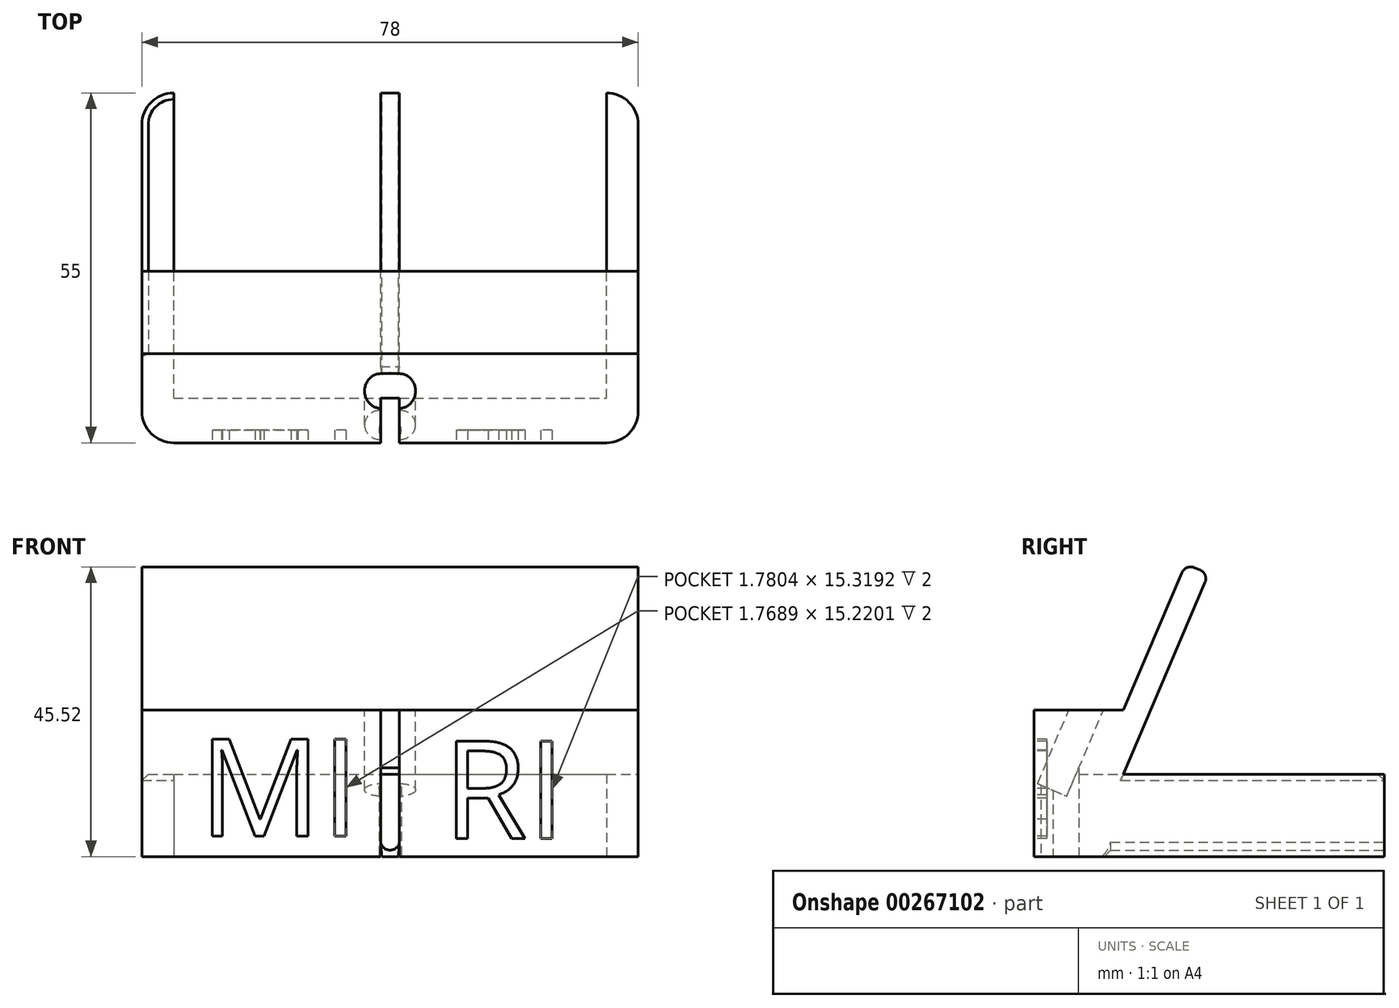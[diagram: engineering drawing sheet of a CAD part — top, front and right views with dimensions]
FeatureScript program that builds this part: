
annotation { "Feature Type Name" : "Feature", "Feature Type Description" : "" }
export const myFeature = defineFeature(function(context is Context, id is Id, definition is map)
    precondition{}
    {
        {
            var Q0;
            Q0=qCreatedBy(makeId("Top.planeOp"),FACE);
            var sketch = newSketch(context, id + "F0", { "sketchPlane" : qUnion([Q0])});
            skLineSegment(sketch, "E0.bottom", {"start": v(-34, 27.5) * mm, "end": v(34, 27.5) * mm});
            skLineSegment(sketch, "E0.top", {"start": v(-34, -27.5) * mm, "end": v(34, -27.5) * mm});
            skLineSegment(sketch, "E0.left", {"start": v(-39, 22.5) * mm, "end": v(-39, -22.5) * mm});
            skLineSegment(sketch, "E0.right", {"start": v(39, 22.5) * mm, "end": v(39, -22.5) * mm});
            skPoint(sketch, "E1.visualSharp", {"position": v(-39, 27.5) * mm});
            skArc(sketch, "E1.filletArc", {"start": v(-34, 27.5) * mm, "mid": v(-37.54, 26.04) * mm, "end": v(-39, 22.5) * mm});
            skPoint(sketch, "E2.visualSharp", {"position": v(39, 27.5) * mm});
            skArc(sketch, "E2.filletArc", {"start": v(39, 22.5) * mm, "mid": v(37.54, 26.04) * mm, "end": v(34, 27.5) * mm});
            skPoint(sketch, "E3.visualSharp", {"position": v(39, -27.5) * mm});
            skArc(sketch, "E3.filletArc", {"start": v(34, -27.5) * mm, "mid": v(37.54, -26.04) * mm, "end": v(39, -22.5) * mm});
            skPoint(sketch, "E4.visualSharp", {"position": v(-39, -27.5) * mm});
            skArc(sketch, "E4.filletArc", {"start": v(-39, -22.5) * mm, "mid": v(-37.54, -26.04) * mm, "end": v(-34, -27.5) * mm});
            skLineSegment(sketch, "E5", {"start": v(0, 27.5) * mm, "end": v(0, -27.5) * mm, "construction": true});
            skSolve(sketch);
        }
        {
            var Q0;
            Q0=makeQuery(id+"F0.imprint","IMPRINT",FACE,{"disambiguationData":[TD([[makeQuery(id+"F0.imprint","IMPRINT",EDGE,{"derivedFrom":sQuery(id+"F0.wireOp",EDGE,"E0.bottom")}),-1.0]])]});
            extrude(context, id + "F1", {"entities" : qUnion([Q0]), "depth" : 50 * mm});
        }
        {
            var Q0;
            Q0=makeQuery(id+"F1.opExtrude","SWEPT_FACE",FACE,{"disambiguationData":[OSD([sQuery(id+"F0.wireOp",EDGE,"E0.right")])]});
            var sketch = newSketch(context, id + "F2", { "sketchPlane" : qUnion([Q0])});
            skLineSegment(sketch, "E6", {"start": v(-27.5, 0) * mm, "end": v(-27.5, 23) * mm, "construction": true});
            skLineSegment(sketch, "E7", {"start": v(-27.5, 23) * mm, "end": v(-13.5, 23) * mm});
            skLineSegment(sketch, "E8", {"start": v(-13.5, 23) * mm, "end": v(-3.68, 46) * mm});
            skLineSegment(sketch, "E9", {"start": v(-13.5, 12.95) * mm, "end": v(27.5, 12.95) * mm});
            skLineSegment(sketch, "E10", {"start": v(27.5, 12.95) * mm, "end": v(27.5, 50) * mm});
            skLineSegment(sketch, "E11", {"start": v(27.5, 50) * mm, "end": v(-27.5, 50) * mm});
            skLineSegment(sketch, "E12", {"start": v(-27.5, 50) * mm, "end": v(-27.5, 23) * mm});
            skLineSegment(sketch, "E13", {"start": v(-3.68, 46) * mm, "end": v(-0.05, 44.44) * mm});
            skLineSegment(sketch, "E14", {"start": v(-0.05, 44.44) * mm, "end": v(-13.5, 12.95) * mm});
            skSolve(sketch);
        }
        {
            var Q0;
            Q0 = qSketchRegion(id + "F2", true);
            extrude(context, id + "F3", {"entities" : qUnion([Q0]), "operationType" : NewBodyOperationType.REMOVE, "endBound" : BoundingType.THROUGH_ALL, "oppositeDirection" : true, "depth" : 25 * mm});
        }
        {
            var Q0;
            Q0=makeQuery(id+"F3.boolean.opBoolean","COPY",EDGE,{"derivedFrom":makeQuery(id+"F3.opExtrude","SWEPT_EDGE",EDGE,{"disambiguationData":[OSD([sQuery(id+"F2.wireOp",EDGE,"E8"),sQuery(id+"F2.wireOp",EDGE,"E13")])]})});
            var Q1;
            Q1=makeQuery(id+"F3.boolean.opBoolean","COPY",EDGE,{"derivedFrom":makeQuery(id+"F3.opExtrude","SWEPT_EDGE",EDGE,{"disambiguationData":[OSD([sQuery(id+"F2.wireOp",EDGE,"E13"),sQuery(id+"F2.wireOp",EDGE,"E14")])]})});
            fillet(context, id + "F4", {"entities" : qUnion([Q0, Q1]), "radius" : 1.5 * mm, "tangentPropagation" : true, "allowEdgeOverflow" : false});
        }
        {
            var Q0;
            Q0=makeQuery(id+"F1.opExtrude","SWEPT_FACE",FACE,{"disambiguationData":[OSD([sQuery(id+"F0.wireOp",EDGE,"E0.bottom")])]});
            var sketch = newSketch(context, id + "F5", { "sketchPlane" : qUnion([Q0])});
            skCircle(sketch, "E15", {"center": v(0, 2.5) * mm, "radius": 1.5 * mm});
            skLineSegment(sketch, "E16", {"start": v(0, 2.5) * mm, "end": v(1.5, 2.5) * mm, "construction": true});
            skLineSegment(sketch, "E17", {"start": v(0, 2.5) * mm, "end": v(-1.5, 2.5) * mm, "construction": true});
            skLineSegment(sketch, "E18", {"start": v(-1.5, 2.5) * mm, "end": v(-1.5, 0) * mm, "construction": true});
            skLineSegment(sketch, "E19", {"start": v(1.5, 2.5) * mm, "end": v(1.5, 0) * mm, "construction": true});
            skLineSegment(sketch, "E20", {"start": v(1.5, 2.5) * mm, "end": v(1.3, 0) * mm});
            skLineSegment(sketch, "E21", {"start": v(-1.5, 2.5) * mm, "end": v(-1.3, 0) * mm});
            skSolve(sketch);
        }
        {
            var Q0;
            Q0 = qSketchRegion(id + "F5", true);
            var Q1;
            {var subQ0=sQuery(id+"F5.wireOp",EDGE,"E18");Q1=makeQuery(id+"F5.imprint","IMPRINT",FACE,{"disambiguationData":[TD([[makeQuery(id+"F5.imprint","IMPRINT",EDGE,{"derivedFrom":subQ0}),1.0]])]});}
            var Q2;
            {var subQ0=sQuery(id+"F5.wireOp",EDGE,"E21");var subQ1=sQuery(id+"F5.wireOp",EDGE,"E15");var subQ2=makeQuery(id+"F5.imprint","INTERSECT",VERTEX,{"disambiguationData":[OD(1.0)],"derivedFrom":[subQ1,subQ0]});Q2=makeQuery(id+"F5.imprint","IMPRINT",FACE,{"disambiguationData":[TD([[makeQuery(id+"F5.imprint","IMPRINT",EDGE,{"disambiguationData":[TD([[subQ2,-1.0]])],"derivedFrom":subQ1}),-1.0]])]});}
            extrude(context, id + "F6", {"entities" : qUnion([Q0, Q1, Q2]), "operationType" : NewBodyOperationType.REMOVE, "oppositeDirection" : true, "depth" : 48 * mm});
        }
        {
            var Q0;
            Q0=makeQuery(id+"F1.opExtrude","SWEPT_FACE",FACE,{"disambiguationData":[OSD([sQuery(id+"F0.wireOp",EDGE,"E0.top")])]});
            var sketch = newSketch(context, id + "F7", { "sketchPlane" : qUnion([Q0])});
            skLineSegment(sketch, "E22", {"start": v(-1.48, 23) * mm, "end": v(1.48, 23) * mm});
            skLineSegment(sketch, "E23", {"start": v(1.48, 23) * mm, "end": v(1.48, 0) * mm});
            skLineSegment(sketch, "E24", {"start": v(1.48, 0) * mm, "end": v(-1.48, 0) * mm});
            skLineSegment(sketch, "E25", {"start": v(-1.48, 23) * mm, "end": v(-1.48, 0) * mm});
            skSolve(sketch);
        }
        {
            var Q0;
            Q0 = qSketchRegion(id + "F7", true);
            extrude(context, id + "F8", {"entities" : qUnion([Q0]), "operationType" : NewBodyOperationType.REMOVE, "oppositeDirection" : true, "depth" : 7 * mm});
        }
        {
            var Q0;
            {var subQ0=sQuery(id+"F0.wireOp",EDGE,"E2.filletArc");var subQ1=sQuery(id+"F0.wireOp",EDGE,"E0.right");var subQ2=sQuery(id+"F0.wireOp",EDGE,"E0.top");var subQ3=sQuery(id+"F0.wireOp",EDGE,"E0.bottom");var subQ4=sQuery(id+"F0.wireOp",EDGE,"E3.filletArc");Q0=makeQuery(id+"F6.boolean.opBoolean","SPLIT",FACE,{"disambiguationData":[TD([makeQuery(id+"F1.opExtrude","SWEPT_FACE",FACE,{"disambiguationData":[OSD([subQ1])]})])],"derivedFrom":makeQuery(id+"F1.opExtrude","CAP_FACE",FACE,{"disambiguationData":[OSD([subQ3,subQ2,sQuery(id+"F0.wireOp",EDGE,"E0.left"),subQ1,sQuery(id+"F0.wireOp",EDGE,"E1.filletArc"),subQ0,subQ4,sQuery(id+"F0.wireOp",EDGE,"E4.filletArc")])],"isStart":true})});}
            var sketch = newSketch(context, id + "F9", { "sketchPlane" : qUnion([Q0])});
            skCircle(sketch, "E26", {"center": v(0, 25.5) * mm, "radius": 1.75 * mm});
            skLineSegment(sketch, "E27", {"start": v(1.5, 27.5) * mm, "end": v(-1.55, 27.5) * mm, "construction": true});
            skSolve(sketch);
        }
        {
            var Q0;
            Q0 = qSketchRegion(id + "F9", true);
            extrude(context, id + "F10", {"entities" : qUnion([Q0]), "operationType" : NewBodyOperationType.REMOVE, "oppositeDirection" : true, "depth" : 12 * mm});
        }
        {
            var Q0;
            Q0=makeQuery(id+"F3.boolean.opBoolean","COPY",FACE,{"derivedFrom":makeQuery(id+"F3.opExtrude","SWEPT_FACE",FACE,{"disambiguationData":[OSD([sQuery(id+"F2.wireOp",EDGE,"E13")])]})});
            var sketch = newSketch(context, id + "F11", { "sketchPlane" : qUnion([Q0])});
            skCircle(sketch, "E28", {"center": v(1.5, -26.82) * mm, "radius": 2.5 * mm});
            skCircle(sketch, "E29", {"center": v(-1.5, -26.82) * mm, "radius": 2.5 * mm});
            skLineSegment(sketch, "E30", {"start": v(1.5, -26.82) * mm, "end": v(-1.5, -26.82) * mm, "construction": true});
            skLineSegment(sketch, "E31", {"start": v(0, 0) * mm, "end": v(0, -37.77) * mm, "construction": true});
            skLineSegment(sketch, "E32", {"start": v(1.5, -26.82) * mm, "end": v(1.5, -24.32) * mm, "construction": true});
            skLineSegment(sketch, "E33", {"start": v(1.5, -24.32) * mm, "end": v(-1.5, -24.32) * mm});
            skLineSegment(sketch, "E34", {"start": v(-1.5, -24.32) * mm, "end": v(-1.5, -29.32) * mm, "construction": true});
            skLineSegment(sketch, "E35", {"start": v(-1.5, -29.32) * mm, "end": v(1.5, -29.32) * mm});
            skLineSegment(sketch, "E36", {"start": v(1.5, -29.32) * mm, "end": v(1.5, -26.82) * mm, "construction": true});
            skLineSegment(sketch, "E37", {"start": v(0, -24.82) * mm, "end": v(0, -29.32) * mm});
            skSolve(sketch);
        }
        {
            var Q0;
            Q0 = qSketchRegion(id + "F11", true);
            var Q1;
            {var subQ0=sQuery(id+"F11.wireOp",EDGE,"E37");var subQ1=sQuery(id+"F11.wireOp",EDGE,"E29");var subQ2=sQuery(id+"F11.wireOp",EDGE,"E28");var subQ3=makeQuery(id+"F11.imprint","INTERSECT",VERTEX,{"disambiguationData":[OD(0.0)],"derivedFrom":[subQ2,subQ1,subQ0]});Q1=makeQuery(id+"F11.imprint","IMPRINT",FACE,{"disambiguationData":[TD([[makeQuery(id+"F11.imprint","IMPRINT",EDGE,{"disambiguationData":[TD([[subQ3,1.0]])],"derivedFrom":subQ1}),1.0]])]});}
            var Q2;
            {var subQ0=sQuery(id+"F11.wireOp",EDGE,"E37");var subQ1=sQuery(id+"F11.wireOp",EDGE,"E29");var subQ2=sQuery(id+"F11.wireOp",EDGE,"E28");var subQ3=makeQuery(id+"F11.imprint","INTERSECT",VERTEX,{"disambiguationData":[OD(0.0)],"derivedFrom":[subQ2,subQ1,subQ0]});Q2=makeQuery(id+"F11.imprint","IMPRINT",FACE,{"disambiguationData":[TD([[makeQuery(id+"F11.imprint","IMPRINT",EDGE,{"disambiguationData":[TD([[subQ3,-1.0]])],"derivedFrom":subQ2}),1.0]])]});}
            extrude(context, id + "F12", {"entities" : qUnion([Q0, Q1, Q2]), "operationType" : NewBodyOperationType.REMOVE, "oppositeDirection" : true, "depth" : 40.9 * mm});
        }
        {
            var Q0;
            {var subQ0=sQuery(id+"F5.wireOp",EDGE,"E15");Q0=makeQuery(id+"F8.boolean.opBoolean","SPLIT",EDGE,{"disambiguationData":[topologyDisambiguationEdgeConnected([makeQuery(id+"F6.boolean.opBoolean","COPY",FACE,{"derivedFrom":makeQuery(id+"F6.opExtrude","SWEPT_FACE",FACE,{"disambiguationData":[OSD([subQ0])]})}),makeQuery(id+"F8.opExtrude","CAP_FACE",FACE,{"disambiguationData":[OSD([sQuery(id+"F7.wireOp",EDGE,"E22"),sQuery(id+"F7.wireOp",EDGE,"E23"),sQuery(id+"F7.wireOp",EDGE,"E24"),sQuery(id+"F7.wireOp",EDGE,"E25")])],"isStart":false})])],"derivedFrom":makeQuery(id+"F6.boolean.opBoolean","COPY",EDGE,{"derivedFrom":makeQuery(id+"F6.opExtrude","CAP_EDGE",EDGE,{"disambiguationData":[OSD([subQ0])],"isStart":false})})});}
            chamfer(context, id + "F13", {"entities" : qUnion([Q0]), "width" : 5 * mm, "tangentPropagation" : true});
        }
        {
            var Q0;
            Q0=makeQuery(id+"F3.boolean.opBoolean","INTERSECT",EDGE,{"derivedFrom":[makeQuery(id+"F1.opExtrude","SWEPT_FACE",FACE,{"disambiguationData":[OSD([sQuery(id+"F0.wireOp",EDGE,"E0.left")])]}),makeQuery(id+"F3.opExtrude","SWEPT_FACE",FACE,{"disambiguationData":[OSD([sQuery(id+"F2.wireOp",EDGE,"E9")])]})]});
            var Q1;
            Q1=makeQuery(id+"F3.boolean.opBoolean","COPY",EDGE,{"derivedFrom":makeQuery(id+"F3.opExtrude","CAP_EDGE",EDGE,{"disambiguationData":[OSD([sQuery(id+"F2.wireOp",EDGE,"E7")])],"isStart":true})});
            var Q2;
            {var subQ0=sQuery(id+"F2.wireOp",EDGE,"E7");Q2=makeQuery(id+"F8.boolean.opBoolean","SPLIT",EDGE,{"disambiguationData":[TD([makeQuery(id+"F1.opExtrude","SWEPT_FACE",FACE,{"disambiguationData":[OSD([sQuery(id+"F0.wireOp",EDGE,"E4.filletArc")])]})])],"derivedFrom":makeQuery(id+"F3.boolean.opBoolean","COPY",EDGE,{"derivedFrom":makeQuery(id+"F3.opExtrude","SWEPT_EDGE",EDGE,{"disambiguationData":[OSD([subQ0,sQuery(id+"F2.wireOp",EDGE,"E12")])]})})});}
            chamfer(context, id + "F14", {"entities" : qUnion([Q0, Q1, Q2]), "width" : 1 * mm, "tangentPropagation" : true});
        }
        {
            var Q0;
            {var subQ0=sQuery(id+"F0.wireOp",EDGE,"E4.filletArc");var subQ1=sQuery(id+"F0.wireOp",EDGE,"E0.top");Q0=makeQuery(id+"F8.boolean.opBoolean","SPLIT",FACE,{"disambiguationData":[TD([makeQuery(id+"F1.opExtrude","SWEPT_FACE",FACE,{"disambiguationData":[OSD([subQ0])]})])],"derivedFrom":makeQuery(id+"F1.opExtrude","SWEPT_FACE",FACE,{"disambiguationData":[OSD([subQ1])]})});}
            var sketch = newSketch(context, id + "F15", { "sketchPlane" : qUnion([Q0])});
            skText(sketch, "E38", { "text": "MI", "fontName": "OpenSans-Regular.ttf"});
            skText(sketch, "E39", { "text": "RI", "fontName": "OpenSans-Regular.ttf"});
            const initialGuessF15  = {"E38": [-0.03006, 0.00324, 1, 0, 0.01535], "E39": [0.00832, 0.00283, 1, 0, 0.01545]};
            skSetInitialGuess(sketch, initialGuessF15);
            skSolve(sketch);
        }
        {
            var Q0;
            Q0=makeQuery(id+"F15.imprint","IMPRINT",FACE,{"disambiguationData":[TD([[makeQuery(id+"F15.imprint","IMPRINT",EDGE,{"derivedFrom":sQuery(id+"F15.wireOp",EDGE,"E38.sketch_text.stroke-18")}),-1.0]])]});
            var Q1;
            Q1=makeQuery(id+"F15.imprint","IMPRINT",FACE,{"disambiguationData":[TD([[makeQuery(id+"F15.imprint","IMPRINT",EDGE,{"derivedFrom":sQuery(id+"F15.wireOp",EDGE,"E38.sketch_text.stroke-0")}),-1.0]])]});
            var Q2;
            Q2=makeQuery(id+"F15.imprint","IMPRINT",FACE,{"disambiguationData":[TD([[makeQuery(id+"F15.imprint","IMPRINT",EDGE,{"derivedFrom":sQuery(id+"F15.wireOp",EDGE,"E39.sketch_text.stroke-0")}),-1.0]])]});
            var Q3;
            Q3=makeQuery(id+"F15.imprint","IMPRINT",FACE,{"disambiguationData":[TD([[makeQuery(id+"F15.imprint","IMPRINT",EDGE,{"derivedFrom":sQuery(id+"F15.wireOp",EDGE,"E39.sketch_text.stroke-18")}),-1.0]])]});
            extrude(context, id + "F16", {"entities" : qUnion([Q0, Q1, Q2, Q3]), "operationType" : NewBodyOperationType.REMOVE, "oppositeDirection" : true, "depth" : 2 * mm});
        }
    });
